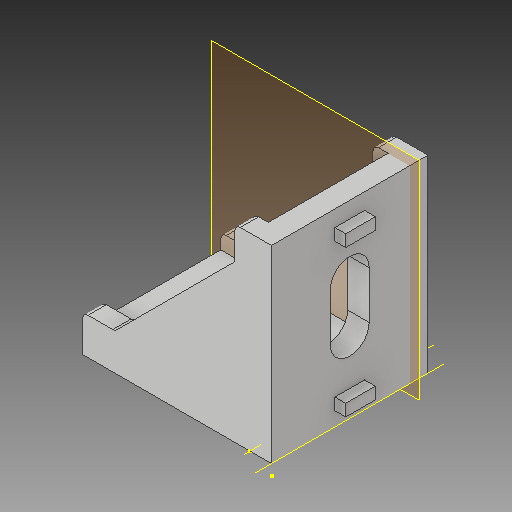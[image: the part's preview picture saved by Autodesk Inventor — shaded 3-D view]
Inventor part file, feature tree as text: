
AUTODESK INVENTOR PART (.ipt)
format: ipt  version: 2017 (Build 210142000, 142)  size: 181,248 bytes
history: native  units: mm
features: sketch x8, other x5, plane x1
ambient origin geometry x8: Origin, YZ Plane, XZ Plane, XY Plane, X Axis, Y Axis, Z Axis, Center Point
bodies: Solid1 (feature_tree)
feature tree (14):
  other  "30mm Bracket_CPY.ipt"
  other  "Solid1::30mm Bracket_CPY.ipt"
  other  "TaggingFeature1"
  sketch  "Sketch1"  dims[d0=10.0mm]
  sketch  "Sketch2"
  sketch  "Sketch3"
  sketch  "Sketch4"
  sketch  "Sketch5"
  sketch  "Sketch7"
  sketch  "Sketch9"
  sketch  "Sketch10"
  plane  "Work Plane1"
  other  "Work Axis1"
  other  "Work Axis2"
